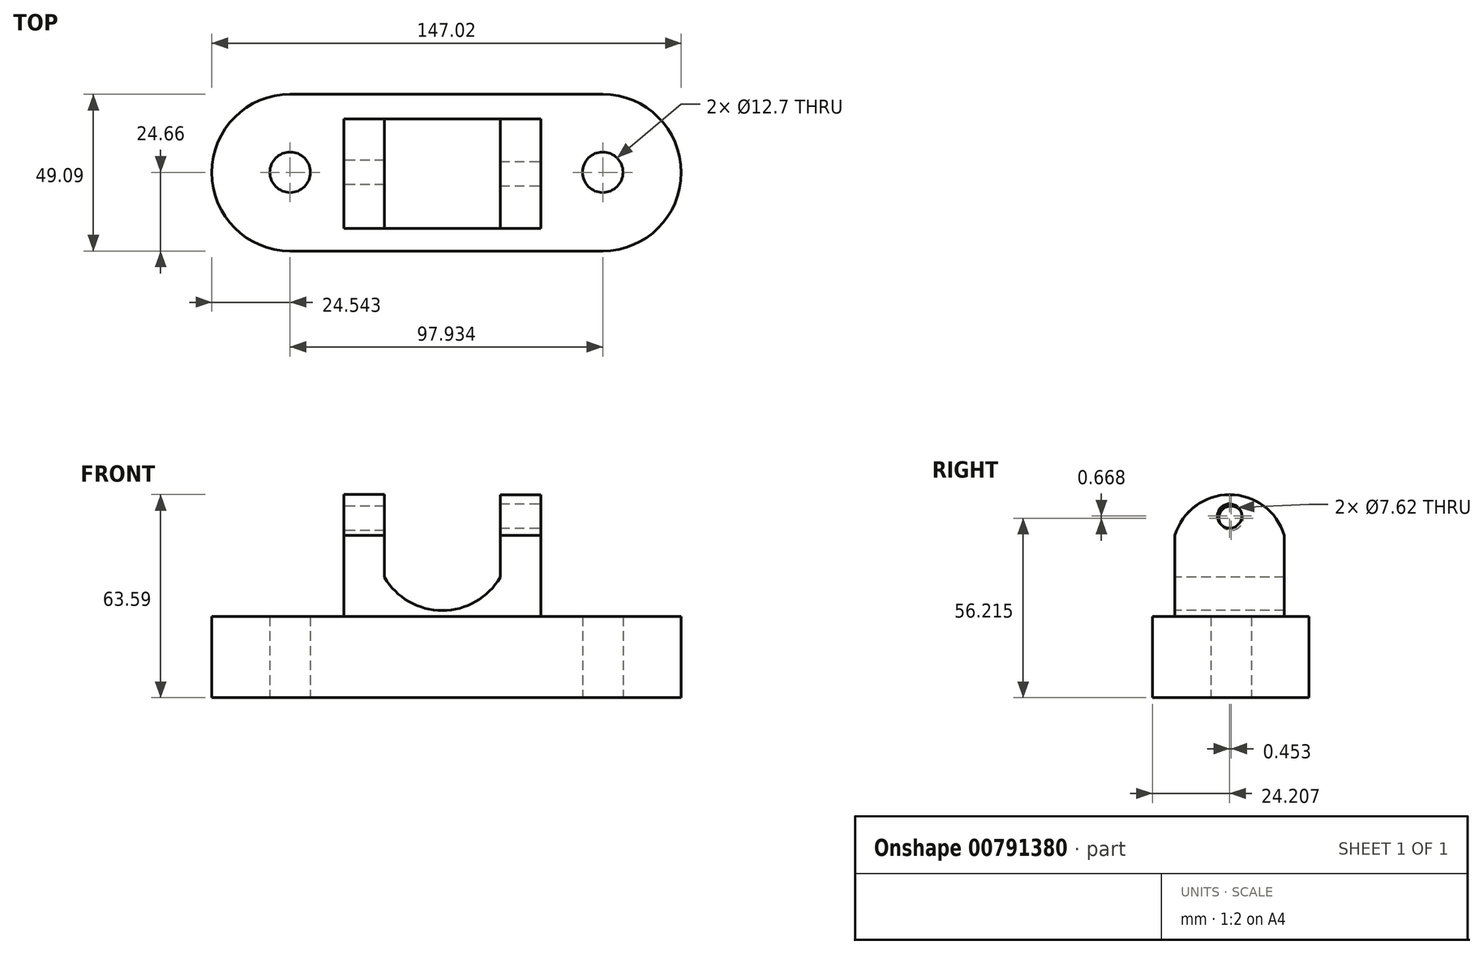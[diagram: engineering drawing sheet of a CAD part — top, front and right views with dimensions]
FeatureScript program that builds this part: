
annotation { "Feature Type Name" : "Feature", "Feature Type Description" : "" }
export const myFeature = defineFeature(function(context is Context, id is Id, definition is map)
    precondition{}
    {
        {
            var Q0;
            Q0=qCreatedBy(makeId("Top.planeOp"),FACE);
            var sketch = newSketch(context, id + "F0", { "sketchPlane" : qUnion([Q0])});
            skLineSegment(sketch, "E0", {"start": v(-48.97, 24.43) * mm, "end": v(48.97, 24.43) * mm});
            skLineSegment(sketch, "E1", {"start": v(-48.97, -24.66) * mm, "end": v(48.97, -24.66) * mm});
            skArc(sketch, "E2", {"start": v(48.97, -24.66) * mm, "mid": v(73.5, -0.12) * mm, "end": v(48.97, 24.43) * mm});
            skArc(sketch, "E3", {"start": v(-48.97, 24.43) * mm, "mid": v(-73.5, -0.12) * mm, "end": v(-48.97, -24.66) * mm});
            skCircle(sketch, "E4", {"center": v(48.97, 0) * mm, "radius": 6.35 * mm});
            skCircle(sketch, "E5", {"center": v(-48.97, 0) * mm, "radius": 6.35 * mm});
            skSolve(sketch);
        }
        {
            var Q0;
            Q0 = qSketchRegion(id + "F0", true);
            extrude(context, id + "F1", {"entities" : qUnion([Q0]), "depth" : 25.4 * mm, "offsetDistance" : 25.4 * mm});
        }
        {
            var Q0;
            Q0=makeQuery(id+"F1.opExtrude","CAP_FACE",FACE,{"disambiguationData":[OSD([sQuery(id+"F0.wireOp",EDGE,"E0"),sQuery(id+"F0.wireOp",EDGE,"E1"),sQuery(id+"F0.wireOp",EDGE,"E2"),sQuery(id+"F0.wireOp",EDGE,"E3"),sQuery(id+"F0.wireOp",EDGE,"E4"),sQuery(id+"F0.wireOp",EDGE,"E5")])],"isStart":false});
            var sketch = newSketch(context, id + "F2", { "sketchPlane" : qUnion([Q0])});
            skLineSegment(sketch, "E6.bottom", {"start": v(-32.14, 16.67) * mm, "end": v(29.55, 16.67) * mm});
            skLineSegment(sketch, "E6.top", {"start": v(-32.14, -17.58) * mm, "end": v(29.55, -17.58) * mm});
            skLineSegment(sketch, "E6.left", {"start": v(-32.14, 16.67) * mm, "end": v(-32.14, -17.58) * mm});
            skLineSegment(sketch, "E6.right", {"start": v(29.55, 16.67) * mm, "end": v(29.55, -17.58) * mm});
            skSolve(sketch);
        }
        {
            var Q0;
            Q0=makeQuery(id+"F2.imprint","IMPRINT",FACE,{"disambiguationData":[TD([[makeQuery(id+"F2.imprint","IMPRINT",EDGE,{"derivedFrom":sQuery(id+"F2.wireOp",EDGE,"E6.bottom")}),-1.0]])]});
            extrude(context, id + "F3", {"entities" : qUnion([Q0]), "operationType" : NewBodyOperationType.ADD, "depth" : 25.4 * mm, "offsetDistance" : 25.4 * mm});
        }
        {
            var Q0;
            Q0=makeQuery(id+"F3.opExtrude","SWEPT_FACE",FACE,{"disambiguationData":[OSD([sQuery(id+"F2.wireOp",EDGE,"E6.top")])]});
            var sketch = newSketch(context, id + "F4", { "sketchPlane" : qUnion([Q0])});
            skLineSegment(sketch, "E7", {"start": v(-32.14, 50.8) * mm, "end": v(-19.44, 50.8) * mm});
            skLineSegment(sketch, "E8", {"start": v(29.55, 50.8) * mm, "end": v(16.85, 50.8) * mm});
            skLineSegment(sketch, "E9", {"start": v(-19.44, 50.8) * mm, "end": v(-19.44, 37.7) * mm});
            skLineSegment(sketch, "E10", {"start": v(16.85, 50.8) * mm, "end": v(16.85, 37.7) * mm});
            skArc(sketch, "E11", {"start": v(-19.44, 37.7) * mm, "mid": v(-1.3, 27.3) * mm, "end": v(16.85, 37.7) * mm});
            skSolve(sketch);
        }
        {
            var Q0;
            {var subQ0=sQuery(id+"F4.wireOp",EDGE,"E9");Q0=makeQuery(id+"F4.imprint","IMPRINT",FACE,{"disambiguationData":[TD([[makeQuery(id+"F4.imprint","IMPRINT",EDGE,{"derivedFrom":subQ0}),1.0]])]});}
            extrude(context, id + "F5", {"entities" : qUnion([Q0]), "operationType" : NewBodyOperationType.REMOVE, "oppositeDirection" : true, "depth" : 36.32 * mm, "offsetDistance" : 25.4 * mm});
        }
        {
            var Q0;
            Q0=makeQuery(id+"F3.opExtrude","SWEPT_FACE",FACE,{"disambiguationData":[OSD([sQuery(id+"F2.wireOp",EDGE,"E6.left")])]});
            var sketch = newSketch(context, id + "F6", { "sketchPlane" : qUnion([Q0])});
            skArc(sketch, "E12", {"start": v(17.58, 50.8) * mm, "mid": v(0.45, 63.6) * mm, "end": v(-16.67, 50.8) * mm});
            skLineSegment(sketch, "E13", {"start": v(-16.67, 50.8) * mm, "end": v(17.58, 50.8) * mm});
            skCircle(sketch, "E14", {"center": v(0, 56.22) * mm, "radius": 3.81 * mm});
            skSolve(sketch);
        }
        {
            var Q0;
            Q0 = qSketchRegion(id + "F6", true);
            extrude(context, id + "F7", {"entities" : qUnion([Q0]), "operationType" : NewBodyOperationType.ADD, "oppositeDirection" : true, "depth" : 12.7 * mm, "offsetDistance" : 25.4 * mm});
        }
        {
            var Q0;
            Q0=makeQuery(id+"F3.opExtrude","SWEPT_FACE",FACE,{"disambiguationData":[OSD([sQuery(id+"F2.wireOp",EDGE,"E6.right")])]});
            var sketch = newSketch(context, id + "F8", { "sketchPlane" : qUnion([Q0])});
            skLineSegment(sketch, "E15", {"start": v(-17.58, 50.8) * mm, "end": v(16.67, 50.8) * mm});
            skArc(sketch, "E16", {"start": v(16.67, 50.8) * mm, "mid": v(-0.45, 63.57) * mm, "end": v(-17.58, 50.8) * mm});
            skCircle(sketch, "E17", {"center": v(-0.45, 56.88) * mm, "radius": 3.81 * mm});
            skPoint(sketch, "E17.centerSnap0", {"position": v(-0.45, 50.8) * mm});
            skSolve(sketch);
        }
        {
            var Q0;
            Q0 = qSketchRegion(id + "F8", true);
            extrude(context, id + "F9", {"entities" : qUnion([Q0]), "operationType" : NewBodyOperationType.ADD, "oppositeDirection" : true, "depth" : 12.7 * mm, "offsetDistance" : 25.4 * mm});
        }
    });
